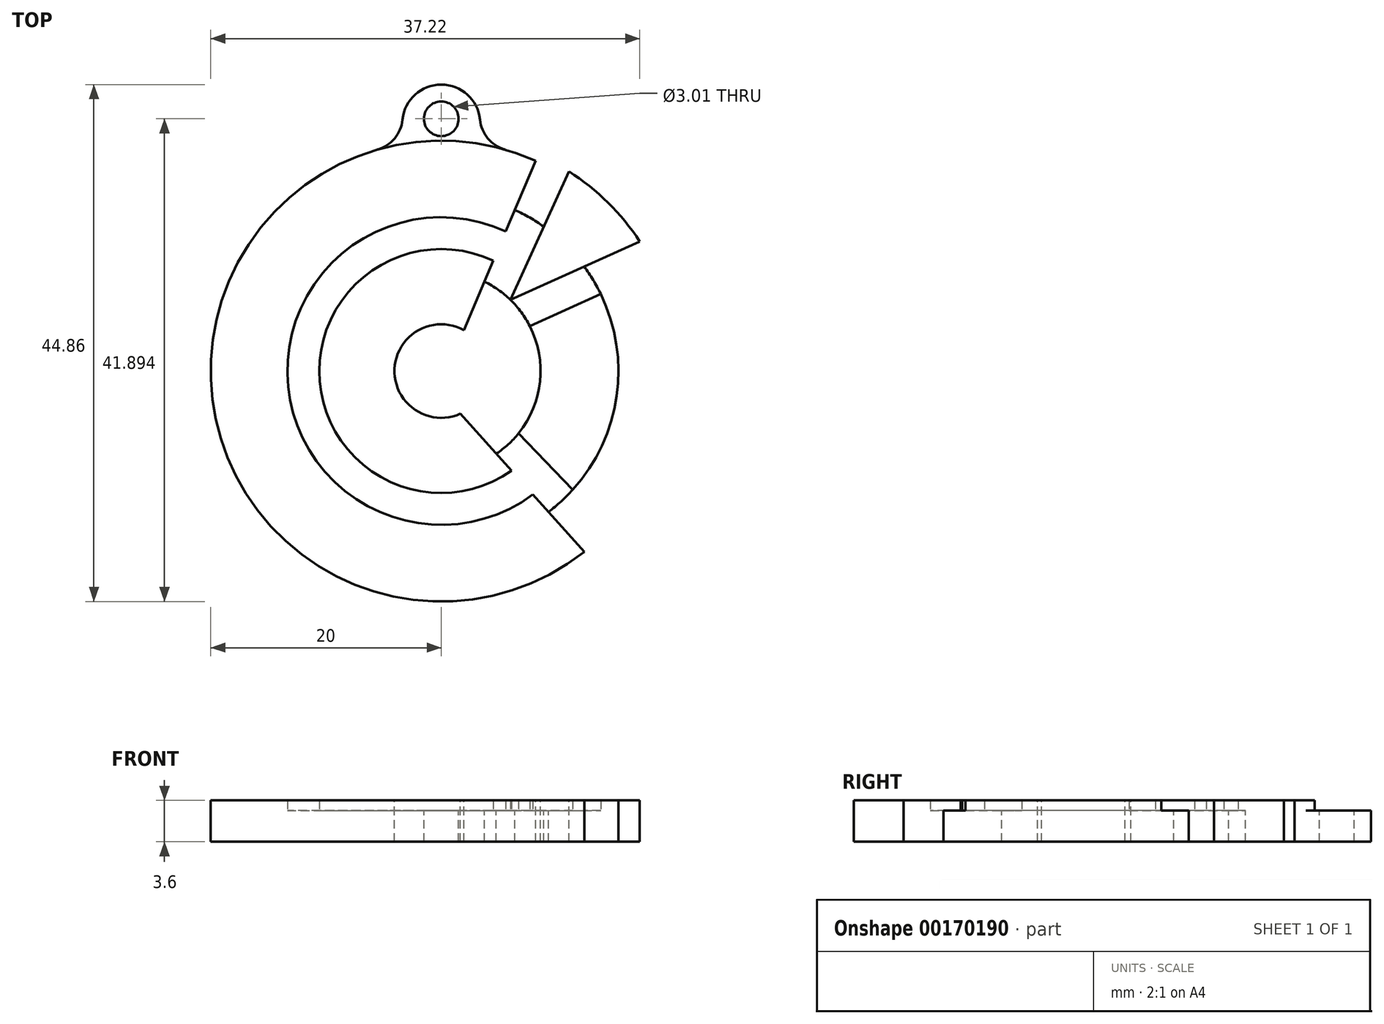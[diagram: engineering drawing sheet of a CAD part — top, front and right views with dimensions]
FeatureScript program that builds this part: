
annotation { "Feature Type Name" : "Feature", "Feature Type Description" : "" }
export const myFeature = defineFeature(function(context is Context, id is Id, definition is map)
    precondition{}
    {
        {
            var Q0;
            Q0=qCreatedBy(makeId("Top.planeOp"),FACE);
            var sketch = newSketch(context, id + "F0", { "sketchPlane" : qUnion([Q0])});
            skCircle(sketch, "E0", {"center": v(0, 0) * mm, "radius": 20 * mm});
            skCircle(sketch, "E1", {"center": v(0, 0) * mm, "radius": 13.35 * mm});
            skCircle(sketch, "E2", {"center": v(0, 0) * mm, "radius": 4.06 * mm});
            skCircle(sketch, "E3", {"center": v(0, 0) * mm, "radius": 10.58 * mm});
            skCircle(sketch, "E4", {"center": v(0, 0) * mm, "radius": 8.61 * mm});
            skCircle(sketch, "E5", {"center": v(0, 0) * mm, "radius": 15.36 * mm});
            skCircle(sketch, "E6", {"center": v(0, 0) * mm, "radius": 20.56 * mm});
            skCircle(sketch, "E7", {"center": v(0, 21.5) * mm, "radius": 3.37 * mm});
            skCircle(sketch, "E8", {"center": v(0, 21.9) * mm, "radius": 1.5 * mm});
            skLineSegment(sketch, "E9", {"start": v(6, 6.18) * mm, "end": v(11.07, 17.32) * mm});
            skLineSegment(sketch, "E10", {"start": v(6, 6.18) * mm, "end": v(17.22, 11.24) * mm});
            skLineSegment(sketch, "E11", {"start": v(8.19, 18.25) * mm, "end": v(1.98, 3.54) * mm});
            skLineSegment(sketch, "E12", {"start": v(1.66, -3.7) * mm, "end": v(12.41, -15.68) * mm});
            skLineSegment(sketch, "E13", {"start": v(7.68, 3.9) * mm, "end": v(13.83, 6.68) * mm});
            skLineSegment(sketch, "E14", {"start": v(11.4, -10.3) * mm, "end": v(6.71, -5.4) * mm});
            skSolve(sketch);
        }
        {
            var Q0;
            {var subQ1=sQuery(id+"F0.wireOp",EDGE,"E0");var subQ4=sQuery(id+"F0.wireOp",EDGE,"E11");var subQ10=makeQuery(id+"F0.imprint","INTERSECT",VERTEX,{"derivedFrom":[subQ1,subQ4]});Q0=makeQuery(id+"F0.imprint","IMPRINT",FACE,{"disambiguationData":[TD([[makeQuery(id+"F0.imprint","IMPRINT",EDGE,{"disambiguationData":[TD([[subQ10,-1.0]])],"derivedFrom":subQ1}),1.0]])]});}
            var Q1;
            {var subQ0=sQuery(id+"F0.wireOp",EDGE,"E11");var subQ1=sQuery(id+"F0.wireOp",EDGE,"E1");var subQ2=makeQuery(id+"F0.imprint","INTERSECT",VERTEX,{"derivedFrom":[subQ1,subQ0]});Q1=makeQuery(id+"F0.imprint","IMPRINT",FACE,{"disambiguationData":[TD([[makeQuery(id+"F0.imprint","IMPRINT",EDGE,{"disambiguationData":[TD([[subQ2,-1.0]])],"derivedFrom":subQ1}),-1.0]])]});}
            var Q2;
            {var subQ0=sQuery(id+"F0.wireOp",EDGE,"E11");var subQ1=sQuery(id+"F0.wireOp",EDGE,"E1");var subQ2=makeQuery(id+"F0.imprint","INTERSECT",VERTEX,{"derivedFrom":[subQ1,subQ0]});Q2=makeQuery(id+"F0.imprint","IMPRINT",FACE,{"disambiguationData":[TD([[makeQuery(id+"F0.imprint","IMPRINT",EDGE,{"disambiguationData":[TD([[subQ2,-1.0]])],"derivedFrom":subQ1}),1.0]])]});}
            var Q3;
            {var subQ0=sQuery(id+"F0.wireOp",EDGE,"E11");var subQ1=sQuery(id+"F0.wireOp",EDGE,"E3");var subQ2=makeQuery(id+"F0.imprint","INTERSECT",VERTEX,{"derivedFrom":[subQ1,subQ0]});Q3=makeQuery(id+"F0.imprint","IMPRINT",FACE,{"disambiguationData":[TD([[makeQuery(id+"F0.imprint","IMPRINT",EDGE,{"disambiguationData":[TD([[subQ2,-1.0]])],"derivedFrom":subQ1}),1.0]])]});}
            var Q4;
            {var subQ0=sQuery(id+"F0.wireOp",EDGE,"E11");var subQ1=sQuery(id+"F0.wireOp",EDGE,"E2");var subQ2=makeQuery(id+"F0.imprint","INTERSECT",VERTEX,{"derivedFrom":[subQ1,subQ0]});Q4=makeQuery(id+"F0.imprint","IMPRINT",FACE,{"disambiguationData":[TD([[makeQuery(id+"F0.imprint","IMPRINT",EDGE,{"disambiguationData":[TD([[subQ2,-1.0]])],"derivedFrom":subQ1}),-1.0]])]});}
            var Q5;
            {var subQ0=sQuery(id+"F0.wireOp",EDGE,"E7");var subQ1=sQuery(id+"F0.wireOp",EDGE,"E0");var subQ2=makeQuery(id+"F0.imprint","INTERSECT",VERTEX,{"disambiguationData":[OD(0.0)],"derivedFrom":[subQ1,subQ0]});Q5=makeQuery(id+"F0.imprint","IMPRINT",FACE,{"disambiguationData":[TD([[makeQuery(id+"F0.imprint","IMPRINT",EDGE,{"disambiguationData":[TD([[subQ2,-1.0]])],"derivedFrom":subQ1}),1.0]])]});}
            var Q6;
            {var subQ0=sQuery(id+"F0.wireOp",EDGE,"E7");var subQ1=sQuery(id+"F0.wireOp",EDGE,"E0");var subQ2=makeQuery(id+"F0.imprint","INTERSECT",VERTEX,{"disambiguationData":[OD(0.0)],"derivedFrom":[subQ1,subQ0]});Q6=makeQuery(id+"F0.imprint","IMPRINT",FACE,{"disambiguationData":[TD([[makeQuery(id+"F0.imprint","IMPRINT",EDGE,{"disambiguationData":[TD([[subQ2,-1.0]])],"derivedFrom":subQ1}),-1.0]])]});}
            var Q7;
            Q7=makeQuery(id+"F0.imprint","IMPRINT",FACE,{"disambiguationData":[TD([[makeQuery(id+"F0.imprint","IMPRINT",EDGE,{"derivedFrom":sQuery(id+"F0.wireOp",EDGE,"E8")}),-1.0]])]});
            var Q8;
            {var subQ0=sQuery(id+"F0.wireOp",EDGE,"E10");var subQ1=sQuery(id+"F0.wireOp",EDGE,"E1");var subQ2=makeQuery(id+"F0.imprint","INTERSECT",VERTEX,{"derivedFrom":[subQ1,subQ0]});Q8=makeQuery(id+"F0.imprint","IMPRINT",FACE,{"disambiguationData":[TD([[makeQuery(id+"F0.imprint","IMPRINT",EDGE,{"disambiguationData":[TD([[subQ2,1.0]])],"derivedFrom":subQ1}),-1.0]])]});}
            var Q9;
            {var subQ0=sQuery(id+"F0.wireOp",EDGE,"E10");var subQ1=sQuery(id+"F0.wireOp",EDGE,"E1");var subQ2=makeQuery(id+"F0.imprint","INTERSECT",VERTEX,{"derivedFrom":[subQ1,subQ0]});Q9=makeQuery(id+"F0.imprint","IMPRINT",FACE,{"disambiguationData":[TD([[makeQuery(id+"F0.imprint","IMPRINT",EDGE,{"disambiguationData":[TD([[subQ2,1.0]])],"derivedFrom":subQ1}),1.0]])]});}
            var Q10;
            {var subQ0=sQuery(id+"F0.wireOp",EDGE,"E10");var subQ1=sQuery(id+"F0.wireOp",EDGE,"E3");var subQ2=makeQuery(id+"F0.imprint","INTERSECT",VERTEX,{"derivedFrom":[subQ1,subQ0]});Q10=makeQuery(id+"F0.imprint","IMPRINT",FACE,{"disambiguationData":[TD([[makeQuery(id+"F0.imprint","IMPRINT",EDGE,{"disambiguationData":[TD([[subQ2,1.0]])],"derivedFrom":subQ1}),1.0]])]});}
            var Q11;
            {var subQ0=sQuery(id+"F0.wireOp",EDGE,"E9");var subQ1=sQuery(id+"F0.wireOp",EDGE,"E3");var subQ2=makeQuery(id+"F0.imprint","INTERSECT",VERTEX,{"derivedFrom":[subQ1,subQ0]});Q11=makeQuery(id+"F0.imprint","IMPRINT",FACE,{"disambiguationData":[TD([[makeQuery(id+"F0.imprint","IMPRINT",EDGE,{"disambiguationData":[TD([[subQ2,1.0]])],"derivedFrom":subQ1}),1.0]])]});}
            var Q12;
            {var subQ0=sQuery(id+"F0.wireOp",EDGE,"E9");var subQ1=sQuery(id+"F0.wireOp",EDGE,"E3");var subQ2=makeQuery(id+"F0.imprint","INTERSECT",VERTEX,{"derivedFrom":[subQ1,subQ0]});Q12=makeQuery(id+"F0.imprint","IMPRINT",FACE,{"disambiguationData":[TD([[makeQuery(id+"F0.imprint","IMPRINT",EDGE,{"disambiguationData":[TD([[subQ2,-1.0]])],"derivedFrom":subQ1}),1.0]])]});}
            var Q13;
            {var subQ0=sQuery(id+"F0.wireOp",EDGE,"E9");var subQ1=sQuery(id+"F0.wireOp",EDGE,"E1");var subQ2=makeQuery(id+"F0.imprint","INTERSECT",VERTEX,{"derivedFrom":[subQ1,subQ0]});Q13=makeQuery(id+"F0.imprint","IMPRINT",FACE,{"disambiguationData":[TD([[makeQuery(id+"F0.imprint","IMPRINT",EDGE,{"disambiguationData":[TD([[subQ2,-1.0]])],"derivedFrom":subQ1}),1.0]])]});}
            var Q14;
            {var subQ0=sQuery(id+"F0.wireOp",EDGE,"E9");var subQ1=sQuery(id+"F0.wireOp",EDGE,"E1");var subQ2=makeQuery(id+"F0.imprint","INTERSECT",VERTEX,{"derivedFrom":[subQ1,subQ0]});Q14=makeQuery(id+"F0.imprint","IMPRINT",FACE,{"disambiguationData":[TD([[makeQuery(id+"F0.imprint","IMPRINT",EDGE,{"disambiguationData":[TD([[subQ2,-1.0]])],"derivedFrom":subQ1}),-1.0]])]});}
            var Q15;
            {var subQ0=sQuery(id+"F0.wireOp",EDGE,"E9");var subQ1=sQuery(id+"F0.wireOp",EDGE,"E1");var subQ2=makeQuery(id+"F0.imprint","INTERSECT",VERTEX,{"derivedFrom":[subQ1,subQ0]});Q15=makeQuery(id+"F0.imprint","IMPRINT",FACE,{"disambiguationData":[TD([[makeQuery(id+"F0.imprint","IMPRINT",EDGE,{"disambiguationData":[TD([[subQ2,1.0]])],"derivedFrom":subQ1}),1.0]])]});}
            var Q16;
            {var subQ0=sQuery(id+"F0.wireOp",EDGE,"E9");var subQ1=sQuery(id+"F0.wireOp",EDGE,"E1");var subQ2=makeQuery(id+"F0.imprint","INTERSECT",VERTEX,{"derivedFrom":[subQ1,subQ0]});Q16=makeQuery(id+"F0.imprint","IMPRINT",FACE,{"disambiguationData":[TD([[makeQuery(id+"F0.imprint","IMPRINT",EDGE,{"disambiguationData":[TD([[subQ2,1.0]])],"derivedFrom":subQ1}),-1.0]])]});}
            var Q17;
            {var subQ0=sQuery(id+"F0.wireOp",EDGE,"E9");var subQ1=sQuery(id+"F0.wireOp",EDGE,"E0");var subQ2=makeQuery(id+"F0.imprint","INTERSECT",VERTEX,{"derivedFrom":[subQ1,subQ0]});Q17=makeQuery(id+"F0.imprint","IMPRINT",FACE,{"disambiguationData":[TD([[makeQuery(id+"F0.imprint","IMPRINT",EDGE,{"disambiguationData":[TD([[subQ2,1.0]])],"derivedFrom":subQ1}),1.0]])]});}
            var Q18;
            {var subQ0=sQuery(id+"F0.wireOp",EDGE,"E9");var subQ1=sQuery(id+"F0.wireOp",EDGE,"E0");var subQ2=makeQuery(id+"F0.imprint","INTERSECT",VERTEX,{"derivedFrom":[subQ1,subQ0]});Q18=makeQuery(id+"F0.imprint","IMPRINT",FACE,{"disambiguationData":[TD([[makeQuery(id+"F0.imprint","IMPRINT",EDGE,{"disambiguationData":[TD([[subQ2,1.0]])],"derivedFrom":subQ1}),-1.0]])]});}
            extrude(context, id + "F1", {"entities" : qUnion([Q0, Q1, Q2, Q3, Q4, Q5, Q6, Q7, Q8, Q9, Q10, Q11, Q12, Q13, Q14, Q15, Q16, Q17, Q18]), "oppositeDirection" : true, "depth" : 2.7 * mm});
        }
        {
            var Q0;
            {var subQ1=sQuery(id+"F0.wireOp",EDGE,"E0");var subQ4=sQuery(id+"F0.wireOp",EDGE,"E11");var subQ10=makeQuery(id+"F0.imprint","INTERSECT",VERTEX,{"derivedFrom":[subQ1,subQ4]});Q0=makeQuery(id+"F0.imprint","IMPRINT",FACE,{"disambiguationData":[TD([[makeQuery(id+"F0.imprint","IMPRINT",EDGE,{"disambiguationData":[TD([[subQ10,-1.0]])],"derivedFrom":subQ1}),1.0]])]});}
            var Q1;
            {var subQ0=sQuery(id+"F0.wireOp",EDGE,"E11");var subQ1=sQuery(id+"F0.wireOp",EDGE,"E1");var subQ2=makeQuery(id+"F0.imprint","INTERSECT",VERTEX,{"derivedFrom":[subQ1,subQ0]});Q1=makeQuery(id+"F0.imprint","IMPRINT",FACE,{"disambiguationData":[TD([[makeQuery(id+"F0.imprint","IMPRINT",EDGE,{"disambiguationData":[TD([[subQ2,-1.0]])],"derivedFrom":subQ1}),-1.0]])]});}
            var Q2;
            {var subQ0=sQuery(id+"F0.wireOp",EDGE,"E11");var subQ1=sQuery(id+"F0.wireOp",EDGE,"E3");var subQ2=makeQuery(id+"F0.imprint","INTERSECT",VERTEX,{"derivedFrom":[subQ1,subQ0]});Q2=makeQuery(id+"F0.imprint","IMPRINT",FACE,{"disambiguationData":[TD([[makeQuery(id+"F0.imprint","IMPRINT",EDGE,{"disambiguationData":[TD([[subQ2,-1.0]])],"derivedFrom":subQ1}),1.0]])]});}
            var Q3;
            {var subQ0=sQuery(id+"F0.wireOp",EDGE,"E11");var subQ1=sQuery(id+"F0.wireOp",EDGE,"E2");var subQ2=makeQuery(id+"F0.imprint","INTERSECT",VERTEX,{"derivedFrom":[subQ1,subQ0]});Q3=makeQuery(id+"F0.imprint","IMPRINT",FACE,{"disambiguationData":[TD([[makeQuery(id+"F0.imprint","IMPRINT",EDGE,{"disambiguationData":[TD([[subQ2,-1.0]])],"derivedFrom":subQ1}),-1.0]])]});}
            var Q4;
            {var subQ0=sQuery(id+"F0.wireOp",EDGE,"E7");var subQ1=sQuery(id+"F0.wireOp",EDGE,"E0");var subQ2=makeQuery(id+"F0.imprint","INTERSECT",VERTEX,{"disambiguationData":[OD(0.0)],"derivedFrom":[subQ1,subQ0]});Q4=makeQuery(id+"F0.imprint","IMPRINT",FACE,{"disambiguationData":[TD([[makeQuery(id+"F0.imprint","IMPRINT",EDGE,{"disambiguationData":[TD([[subQ2,-1.0]])],"derivedFrom":subQ1}),1.0]])]});}
            extrude(context, id + "F2", {"entities" : qUnion([Q0, Q1, Q2, Q3, Q4]), "operationType" : NewBodyOperationType.ADD, "depth" : 0.9 * mm});
        }
        {
            var Q0;
            {var subQ0=sQuery(id+"F0.wireOp",EDGE,"E13");var subQ1=sQuery(id+"F0.wireOp",EDGE,"E3");var subQ2=makeQuery(id+"F0.imprint","INTERSECT",VERTEX,{"derivedFrom":[subQ1,subQ0]});Q0=makeQuery(id+"F0.imprint","IMPRINT",FACE,{"disambiguationData":[TD([[makeQuery(id+"F0.imprint","IMPRINT",EDGE,{"disambiguationData":[TD([[subQ2,1.0]])],"derivedFrom":subQ1}),1.0]])]});}
            var Q1;
            {var subQ0=sQuery(id+"F0.wireOp",EDGE,"E13");var subQ1=sQuery(id+"F0.wireOp",EDGE,"E1");var subQ2=makeQuery(id+"F0.imprint","INTERSECT",VERTEX,{"derivedFrom":[subQ1,subQ0]});Q1=makeQuery(id+"F0.imprint","IMPRINT",FACE,{"disambiguationData":[TD([[makeQuery(id+"F0.imprint","IMPRINT",EDGE,{"disambiguationData":[TD([[subQ2,1.0]])],"derivedFrom":subQ1}),1.0]])]});}
            var Q2;
            {var subQ0=sQuery(id+"F0.wireOp",EDGE,"E13");var subQ1=sQuery(id+"F0.wireOp",EDGE,"E1");var subQ2=makeQuery(id+"F0.imprint","INTERSECT",VERTEX,{"derivedFrom":[subQ1,subQ0]});Q2=makeQuery(id+"F0.imprint","IMPRINT",FACE,{"disambiguationData":[TD([[makeQuery(id+"F0.imprint","IMPRINT",EDGE,{"disambiguationData":[TD([[subQ2,1.0]])],"derivedFrom":subQ1}),-1.0]])]});}
            var Q3;
            {var subQ0=sQuery(id+"F0.wireOp",EDGE,"E12");var subQ1=sQuery(id+"F0.wireOp",EDGE,"E1");var subQ2=makeQuery(id+"F0.imprint","INTERSECT",VERTEX,{"derivedFrom":[subQ1,subQ0]});Q3=makeQuery(id+"F0.imprint","IMPRINT",FACE,{"disambiguationData":[TD([[makeQuery(id+"F0.imprint","IMPRINT",EDGE,{"disambiguationData":[TD([[subQ2,-1.0]])],"derivedFrom":subQ1}),-1.0]])]});}
            var Q4;
            {var subQ0=sQuery(id+"F0.wireOp",EDGE,"E12");var subQ1=sQuery(id+"F0.wireOp",EDGE,"E1");var subQ2=makeQuery(id+"F0.imprint","INTERSECT",VERTEX,{"derivedFrom":[subQ1,subQ0]});Q4=makeQuery(id+"F0.imprint","IMPRINT",FACE,{"disambiguationData":[TD([[makeQuery(id+"F0.imprint","IMPRINT",EDGE,{"disambiguationData":[TD([[subQ2,-1.0]])],"derivedFrom":subQ1}),1.0]])]});}
            var Q5;
            {var subQ0=sQuery(id+"F0.wireOp",EDGE,"E12");var subQ1=sQuery(id+"F0.wireOp",EDGE,"E3");var subQ2=makeQuery(id+"F0.imprint","INTERSECT",VERTEX,{"derivedFrom":[subQ1,subQ0]});Q5=makeQuery(id+"F0.imprint","IMPRINT",FACE,{"disambiguationData":[TD([[makeQuery(id+"F0.imprint","IMPRINT",EDGE,{"disambiguationData":[TD([[subQ2,-1.0]])],"derivedFrom":subQ1}),1.0]])]});}
            extrude(context, id + "F3", {"entities" : qUnion([Q0, Q1, Q2, Q3, Q4, Q5]), "operationType" : NewBodyOperationType.ADD, "oppositeDirection" : true, "depth" : 2.7 * mm});
        }
        {
            var Q0;
            {var subQ0=sQuery(id+"F0.wireOp",EDGE,"E13");var subQ1=sQuery(id+"F0.wireOp",EDGE,"E1");var subQ2=makeQuery(id+"F0.imprint","INTERSECT",VERTEX,{"derivedFrom":[subQ1,subQ0]});Q0=makeQuery(id+"F0.imprint","IMPRINT",FACE,{"disambiguationData":[TD([[makeQuery(id+"F0.imprint","IMPRINT",EDGE,{"disambiguationData":[TD([[subQ2,1.0]])],"derivedFrom":subQ1}),-1.0]])]});}
            var Q1;
            {var subQ0=sQuery(id+"F0.wireOp",EDGE,"E13");var subQ1=sQuery(id+"F0.wireOp",EDGE,"E1");var subQ2=makeQuery(id+"F0.imprint","INTERSECT",VERTEX,{"derivedFrom":[subQ1,subQ0]});Q1=makeQuery(id+"F0.imprint","IMPRINT",FACE,{"disambiguationData":[TD([[makeQuery(id+"F0.imprint","IMPRINT",EDGE,{"disambiguationData":[TD([[subQ2,1.0]])],"derivedFrom":subQ1}),1.0]])]});}
            var Q2;
            {var subQ0=sQuery(id+"F0.wireOp",EDGE,"E13");var subQ1=sQuery(id+"F0.wireOp",EDGE,"E3");var subQ2=makeQuery(id+"F0.imprint","INTERSECT",VERTEX,{"derivedFrom":[subQ1,subQ0]});Q2=makeQuery(id+"F0.imprint","IMPRINT",FACE,{"disambiguationData":[TD([[makeQuery(id+"F0.imprint","IMPRINT",EDGE,{"disambiguationData":[TD([[subQ2,1.0]])],"derivedFrom":subQ1}),1.0]])]});}
            var Q3;
            {var subQ0=sQuery(id+"F0.wireOp",EDGE,"E9");var subQ1=sQuery(id+"F0.wireOp",EDGE,"E0");var subQ2=makeQuery(id+"F0.imprint","INTERSECT",VERTEX,{"derivedFrom":[subQ1,subQ0]});Q3=makeQuery(id+"F0.imprint","IMPRINT",FACE,{"disambiguationData":[TD([[makeQuery(id+"F0.imprint","IMPRINT",EDGE,{"disambiguationData":[TD([[subQ2,1.0]])],"derivedFrom":subQ1}),-1.0]])]});}
            var Q4;
            {var subQ0=sQuery(id+"F0.wireOp",EDGE,"E10");var subQ1=sQuery(id+"F0.wireOp",EDGE,"E3");var subQ2=makeQuery(id+"F0.imprint","INTERSECT",VERTEX,{"derivedFrom":[subQ1,subQ0]});Q4=makeQuery(id+"F0.imprint","IMPRINT",FACE,{"disambiguationData":[TD([[makeQuery(id+"F0.imprint","IMPRINT",EDGE,{"disambiguationData":[TD([[subQ2,-1.0]])],"derivedFrom":subQ1}),1.0]])]});}
            var Q5;
            {var subQ0=sQuery(id+"F0.wireOp",EDGE,"E10");var subQ1=sQuery(id+"F0.wireOp",EDGE,"E1");var subQ2=makeQuery(id+"F0.imprint","INTERSECT",VERTEX,{"derivedFrom":[subQ1,subQ0]});Q5=makeQuery(id+"F0.imprint","IMPRINT",FACE,{"disambiguationData":[TD([[makeQuery(id+"F0.imprint","IMPRINT",EDGE,{"disambiguationData":[TD([[subQ2,-1.0]])],"derivedFrom":subQ1}),1.0]])]});}
            var Q6;
            {var subQ0=sQuery(id+"F0.wireOp",EDGE,"E10");var subQ1=sQuery(id+"F0.wireOp",EDGE,"E1");var subQ2=makeQuery(id+"F0.imprint","INTERSECT",VERTEX,{"derivedFrom":[subQ1,subQ0]});Q6=makeQuery(id+"F0.imprint","IMPRINT",FACE,{"disambiguationData":[TD([[makeQuery(id+"F0.imprint","IMPRINT",EDGE,{"disambiguationData":[TD([[subQ2,-1.0]])],"derivedFrom":subQ1}),-1.0]])]});}
            var Q7;
            {var subQ0=sQuery(id+"F0.wireOp",EDGE,"E9");var subQ1=sQuery(id+"F0.wireOp",EDGE,"E0");var subQ2=makeQuery(id+"F0.imprint","INTERSECT",VERTEX,{"derivedFrom":[subQ1,subQ0]});Q7=makeQuery(id+"F0.imprint","IMPRINT",FACE,{"disambiguationData":[TD([[makeQuery(id+"F0.imprint","IMPRINT",EDGE,{"disambiguationData":[TD([[subQ2,1.0]])],"derivedFrom":subQ1}),1.0]])]});}
            extrude(context, id + "F4", {"entities" : qUnion([Q0, Q1, Q2, Q3, Q4, Q5, Q6, Q7]), "operationType" : NewBodyOperationType.ADD, "depth" : 0.9 * mm});
        }
        {
            var Q0;
            {var subQ0=sQuery(id+"F0.wireOp",EDGE,"E7");var subQ1=sQuery(id+"F0.wireOp",EDGE,"E0");Q0=makeQuery(id+"F1.opExtrude","SWEPT_EDGE",EDGE,{"disambiguationData":[OSD([subQ1,subQ0]),TDD([makeQuery(id+"F0.imprint","INTERSECT",VERTEX,{"disambiguationData":[OD(0.0)],"derivedFrom":[subQ1,subQ0]})])]});}
            var Q1;
            {var subQ0=sQuery(id+"F0.wireOp",EDGE,"E7");var subQ1=sQuery(id+"F0.wireOp",EDGE,"E0");Q1=makeQuery(id+"F1.opExtrude","SWEPT_EDGE",EDGE,{"disambiguationData":[OSD([subQ1,subQ0]),TDD([makeQuery(id+"F0.imprint","INTERSECT",VERTEX,{"disambiguationData":[OD(1.0)],"derivedFrom":[subQ1,subQ0]})])]});}
            fillet(context, id + "F5", {"entities" : qUnion([Q0, Q1]), "radius" : 3 * mm, "tangentPropagation" : true, "allowEdgeOverflow" : false});
        }
        {
            var Q0;
            Q0=makeQuery(id+"F4.opExtrude","CAP_FACE",FACE,{"disambiguationData":[OSD([sQuery(id+"F0.wireOp",EDGE,"E4"),sQuery(id+"F0.wireOp",EDGE,"E5"),sQuery(id+"F0.wireOp",EDGE,"E13"),sQuery(id+"F0.wireOp",EDGE,"E14")])],"isStart":false});
            var Q1;
            Q1=makeQuery(id+"F4.opExtrude","CAP_FACE",FACE,{"disambiguationData":[OSD([sQuery(id+"F0.wireOp",EDGE,"E6"),sQuery(id+"F0.wireOp",EDGE,"E9"),sQuery(id+"F0.wireOp",EDGE,"E10")])],"isStart":false});
            extrude(context, id + "F6", {"entities" : qUnion([Q0, Q1]), "depth" : .9 * mm});
        }
        {
            var Q0;
            Q0=makeQuery(id+"F6.opExtrude","SWEPT_BODY",BODY,{"disambiguationData":[OSD([sQuery(id+"F0.wireOp",EDGE,"E4"),sQuery(id+"F0.wireOp",EDGE,"E5"),sQuery(id+"F0.wireOp",EDGE,"E13"),sQuery(id+"F0.wireOp",EDGE,"E14")])]});
            deleteBodies(context, id + "F7", {"entities" : qUnion([Q0])});
        }
        {
            var Q0;
            Q0=makeQuery(id+"F6.opExtrude","SWEPT_BODY",BODY,{"disambiguationData":[OSD([sQuery(id+"F0.wireOp",EDGE,"E6"),sQuery(id+"F0.wireOp",EDGE,"E9"),sQuery(id+"F0.wireOp",EDGE,"E10")])]});
            deleteBodies(context, id + "F8", {"entities" : qUnion([Q0])});
        }
    });
